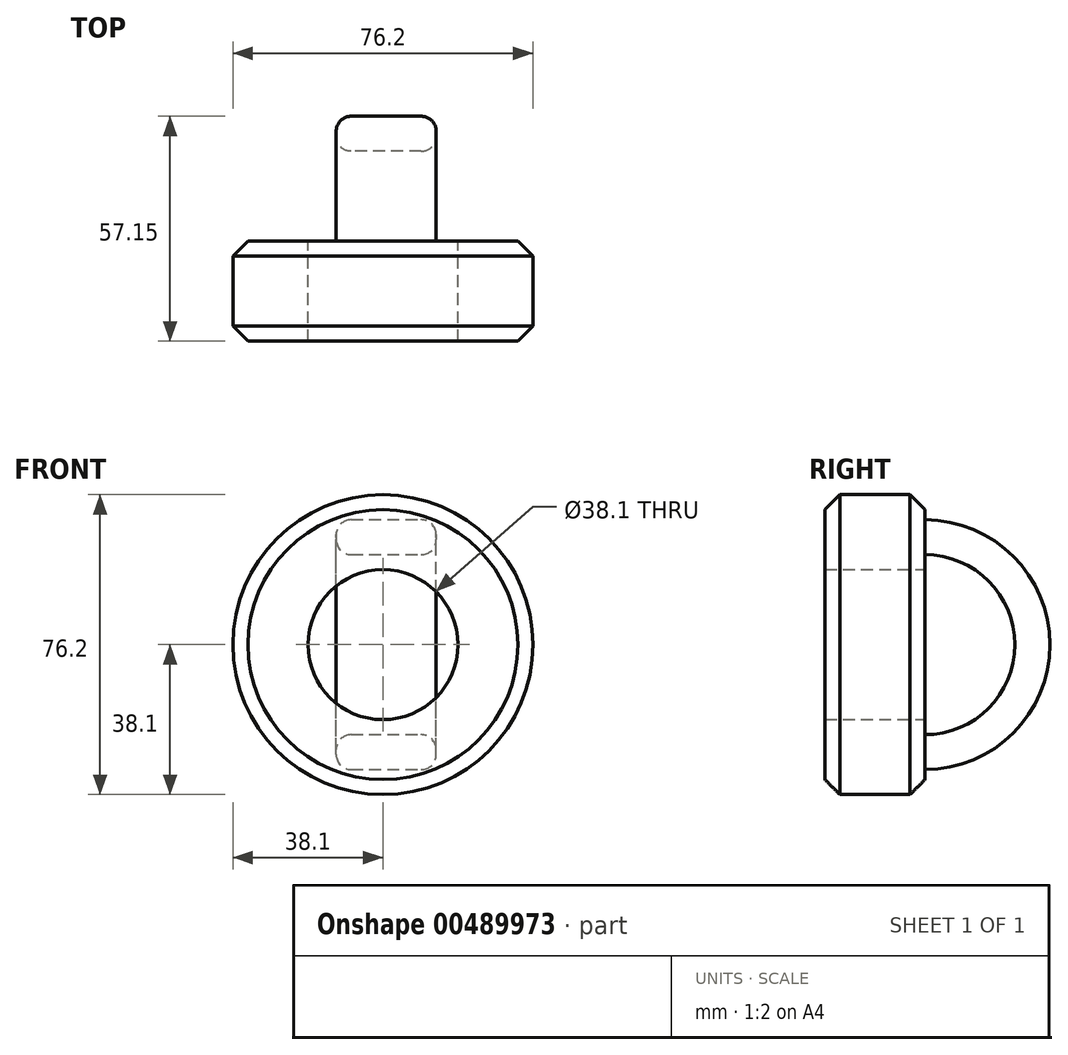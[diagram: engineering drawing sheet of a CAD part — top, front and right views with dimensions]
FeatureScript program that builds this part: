
annotation { "Feature Type Name" : "Feature", "Feature Type Description" : "" }
export const myFeature = defineFeature(function(context is Context, id is Id, definition is map)
    precondition{}
    {
        {
            var Q0;
            Q0=qCreatedBy(makeId("Front.planeOp"),FACE);
            var sketch = newSketch(context, id + "F0", { "sketchPlane" : qUnion([Q0])});
            skCircle(sketch, "E0", {"center": v(0, 0) * mm, "radius": 19.05 * mm});
            skCircle(sketch, "E1", {"center": v(0, 0) * mm, "radius": 38.1 * mm});
            skSolve(sketch);
        }
        {
            var Q0;
            Q0=makeQuery(id+"F0.imprint","IMPRINT",FACE,{"disambiguationData":[TD([[makeQuery(id+"F0.imprint","IMPRINT",EDGE,{"derivedFrom":sQuery(id+"F0.wireOp",EDGE,"E0")}),-1.0]])]});
            extrude(context, id + "F1", {"entities" : qUnion([Q0]), "depth" : 25.4 * mm});
        }
        {
            var Q0;
            Q0=qCreatedBy(makeId("Front.planeOp"),FACE);
            var sketch = newSketch(context, id + "F2", { "sketchPlane" : qUnion([Q0])});
            skLineSegment(sketch, "E2", {"start": v(-80.62, 0) * mm, "end": v(80.93, 0) * mm});
            skLineSegment(sketch, "E3.bottom", {"start": v(-11.87, 31.75) * mm, "end": v(13.53, 31.75) * mm});
            skLineSegment(sketch, "E3.top", {"start": v(-11.87, 22.86) * mm, "end": v(13.53, 22.86) * mm});
            skLineSegment(sketch, "E3.left", {"start": v(-11.87, 31.75) * mm, "end": v(-11.87, 22.86) * mm});
            skLineSegment(sketch, "E3.right", {"start": v(13.53, 31.75) * mm, "end": v(13.53, 22.86) * mm});
            skLineSegment(sketch, "E4.bottom", {"start": v(-11.87, -31.75) * mm, "end": v(13.53, -31.75) * mm});
            skLineSegment(sketch, "E4.top", {"start": v(-11.87, -22.86) * mm, "end": v(13.53, -22.86) * mm});
            skLineSegment(sketch, "E4.left", {"start": v(-11.87, -31.75) * mm, "end": v(-11.87, -22.86) * mm});
            skLineSegment(sketch, "E4.right", {"start": v(13.53, -31.75) * mm, "end": v(13.53, -22.86) * mm});
            skSolve(sketch);
        }
        {
            var Q0;
            Q0=makeQuery(id+"F2.imprint","IMPRINT",FACE,{"disambiguationData":[TD([[makeQuery(id+"F2.imprint","IMPRINT",EDGE,{"derivedFrom":sQuery(id+"F2.wireOp",EDGE,"E4.bottom")}),1.0]])]});
            var Q1;
            Q1=sQuery(id+"F2.wireOp",EDGE,"E2");
            revolve(context, id + "F3", {"operationType" : NewBodyOperationType.ADD, "entities" : qUnion([Q0]), "axis" : qUnion([Q1]), "revolveType" : RevolveType.ONE_DIRECTION, "angle" : 180 * degree});
        }
        {
            var Q0;
            Q0=makeQuery(id+"F3.opRevolve","SWEPT_EDGE",EDGE,{"disambiguationData":[OSD([sQuery(id+"F2.wireOp",EDGE,"E4.bottom"),sQuery(id+"F2.wireOp",EDGE,"E4.right")])]});
            var Q1;
            Q1=makeQuery(id+"F3.opRevolve","SWEPT_EDGE",EDGE,{"disambiguationData":[OSD([sQuery(id+"F2.wireOp",EDGE,"E4.bottom"),sQuery(id+"F2.wireOp",EDGE,"E4.left")])]});
            var Q2;
            Q2=makeQuery(id+"F3.opRevolve","SWEPT_EDGE",EDGE,{"disambiguationData":[OSD([sQuery(id+"F2.wireOp",EDGE,"E4.top"),sQuery(id+"F2.wireOp",EDGE,"E4.left")])]});
            var Q3;
            Q3=makeQuery(id+"F3.opRevolve","SWEPT_EDGE",EDGE,{"disambiguationData":[OSD([sQuery(id+"F2.wireOp",EDGE,"E4.top"),sQuery(id+"F2.wireOp",EDGE,"E4.right")])]});
            fillet(context, id + "F4", {"entities" : qUnion([Q0, Q1, Q2, Q3]), "radius" : 3.8 * mm, "tangentPropagation" : true, "allowEdgeOverflow" : false});
        }
        {
            var Q0;
            Q0=makeQuery(id+"F1.opExtrude","CAP_EDGE",EDGE,{"disambiguationData":[OSD([sQuery(id+"F0.wireOp",EDGE,"E1")])],"isStart":true});
            var Q1;
            Q1=makeQuery(id+"F1.opExtrude","CAP_EDGE",EDGE,{"disambiguationData":[OSD([sQuery(id+"F0.wireOp",EDGE,"E1")])],"isStart":false});
            chamfer(context, id + "F5", {"entities" : qUnion([Q0, Q1]), "width" : 3.8 * mm, "tangentPropagation" : true});
        }
    });
